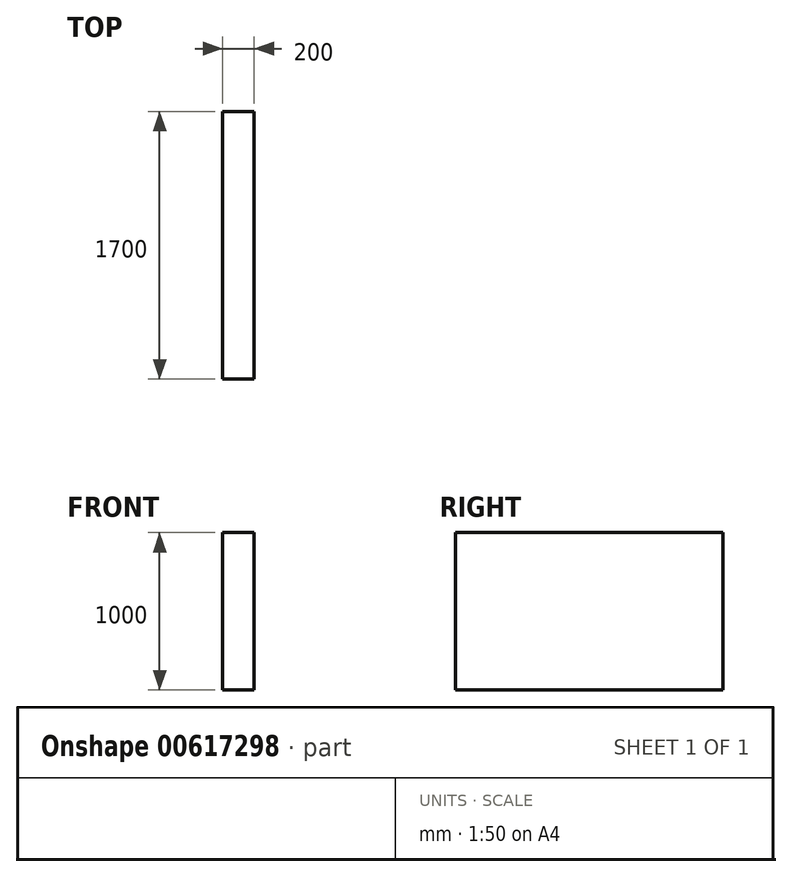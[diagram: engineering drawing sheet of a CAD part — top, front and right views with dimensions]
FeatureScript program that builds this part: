
annotation { "Feature Type Name" : "Feature", "Feature Type Description" : "" }
export const myFeature = defineFeature(function(context is Context, id is Id, definition is map)
    precondition{}
    {
        {
            var Q0;
            Q0=qCreatedBy(makeId("Top.planeOp"),FACE);
            var sketch = newSketch(context, id + "F0", { "sketchPlane" : qUnion([Q0])});
            skLineSegment(sketch, "E0.bottom", {"start": v(-90.53, 1582.2) * mm, "end": v(109.47, 1582.2) * mm});
            skLineSegment(sketch, "E0.top", {"start": v(-90.53, -117.8) * mm, "end": v(109.47, -117.8) * mm});
            skLineSegment(sketch, "E0.left", {"start": v(-90.53, 1582.2) * mm, "end": v(-90.53, -117.8) * mm});
            skLineSegment(sketch, "E0.right", {"start": v(109.47, 1582.2) * mm, "end": v(109.47, -117.8) * mm});
            skSolve(sketch);
        }
        {
            var Q0;
            Q0 = qSketchRegion(id + "F0", true);
            extrude(context, id + "F1", {"entities" : qUnion([Q0]), "depth" : 1000 * mm, "offsetDistance" : 25 * mm});
        }
    });
